# Revit family: Viking Roofspec Sump 05 M17
name_source: partatom
category: Pipe Fittings
units: mm (PartAtom-declared; Revit-internal decimal feet)

## family parameters
Cut with Voids When Loaded = No
Host = Face
Part Type = Cap
Round Connector Dimension = Use Diameter
Shared = No

## types (1)
- Sumps IMR130 580x380x249mmd+150mm outlet
    Component = IMR130
    Default Elevation = 0 mm  [stored 0 ft]
    Flange Cut Length = 580 mm  [stored 1.90289 ft]
    Flange Cut Width = 380 mm  [stored 1.24672 ft]
    Flow Out = 7.6 L/s
    Manufacturer = Viking Roofspec
    Material = Viking Roofspec - Plastic White
    Model = IMR130
    Offset Pipe1 = 137 mm
    Offset Pipe2 = 114 mm
    Overall Height = 389 mm  [stored 1.27625 ft]
    Pipe Diameter = 150 mm  [stored 0.492126 ft]
    Type Comments = Viking Roofspec sump / overflow IMR130, installed as per manufacturers instructions.
    URL = www.vikingroofspec.co.nz

note: [stored X ft] marks values corroborated as IEEE doubles in the binary element streams (Revit-internal decimal feet)

## geometry (parser evidence)
native form markers: Sweep x22
no freeform markers — native parametric forms only
